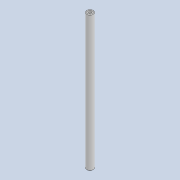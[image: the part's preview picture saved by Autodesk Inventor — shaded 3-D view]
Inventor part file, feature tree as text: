
AUTODESK INVENTOR PART (.ipt)
format: ipt  version: 2020 (Build 240168000, 168)  size: 78,336 bytes
history: native  units: mm
features: extrude x1, chamfer x1, sketch x1
ambient origin geometry x8: Origin, YZ Plane, XZ Plane, XY Plane, X Axis, Y Axis, Z Axis, Center Point
bodies: Solid1 (feature_tree)
feature tree (3):
  extrude  "Extrusion1"  Depth=1.5mm
  chamfer  "Chamfer1"  Distance=60.0mm
  sketch  "Sketch1"  dims[d0=3.0mm d1=1.5mm d2=60.0mm d3=0.0mm d4=0.25mm d5=2.0mm d6=45.0deg]
